# Revit family: DVWN
name_source: partatom
category: Wyposażenie mechaniczne
revit_build: Autodesk Revit 2017 (Build: 20160225_1515(x64)
units: mm (PartAtom-declared; Revit-internal decimal feet)

## family parameters
Oparty na płaszczyźnie roboczej = Nie
Punkt obliczania pomieszczeń = Nie
Tnij formami wycięć po wczytaniu = Nie
Typ części = Normalny
Współdzielony = Nie
Wymiar okrągłego złącza = Użyj średnicy
Zawsze pionowo = Tak

## types (2) — shared parameters
A = 555 mm  [stored 1.82087 ft]
Air_flow = 0.0 m³/h
Current = 1 A
Da = 464 mm  [stored 1.52231 ft]
Date = 11.2018
Di = 402 mm  [stored 1.3189 ft]
Frequency = 50 Hz
H = 900 mm  [stored 2.95276 ft]
Height = 390 mm  [stored 1.27953 ft]
Height_1 = 550 mm
Height_2 = 150 mm  [stored 0.492126 ft]
Iniet_Collar = Tak
L = 220 mm  [stored 0.721785 ft]
P = 817 mm  [stored 2.68045 ft]
Pressure = 0.0 Pa
Producent = Rosenberg
Protection_class = IP55
Shutter_Automatic = Tak
Socket_Sound_Attenuator = Tak
URL = https://www.rosenberg.pl
Version = 1
Voltage = 400 V
W1 = 900 mm  [stored 2.95276 ft]
W2 = 220 mm  [stored 0.721785 ft]
W3 = 220 mm  [stored 0.721785 ft]
Width = 720 mm  [stored 2.3622 ft]
Width_bottom = 595 mm  [stored 1.9521 ft]
max.Ambient_temperature = 120 °C
t1 = 2 mm  [stored 0.00656168 ft]

## per-type parameters (varying)
| type | Power | Weight[kg] |
| 355-4D-120C | 0 kW | 29.5 |
| 400-4D-120C | 1 kW | 30 |

note: column(s) folded — value = type name in every type: Model

note: [stored X ft] marks values corroborated as IEEE doubles in the binary element streams (Revit-internal decimal feet)
